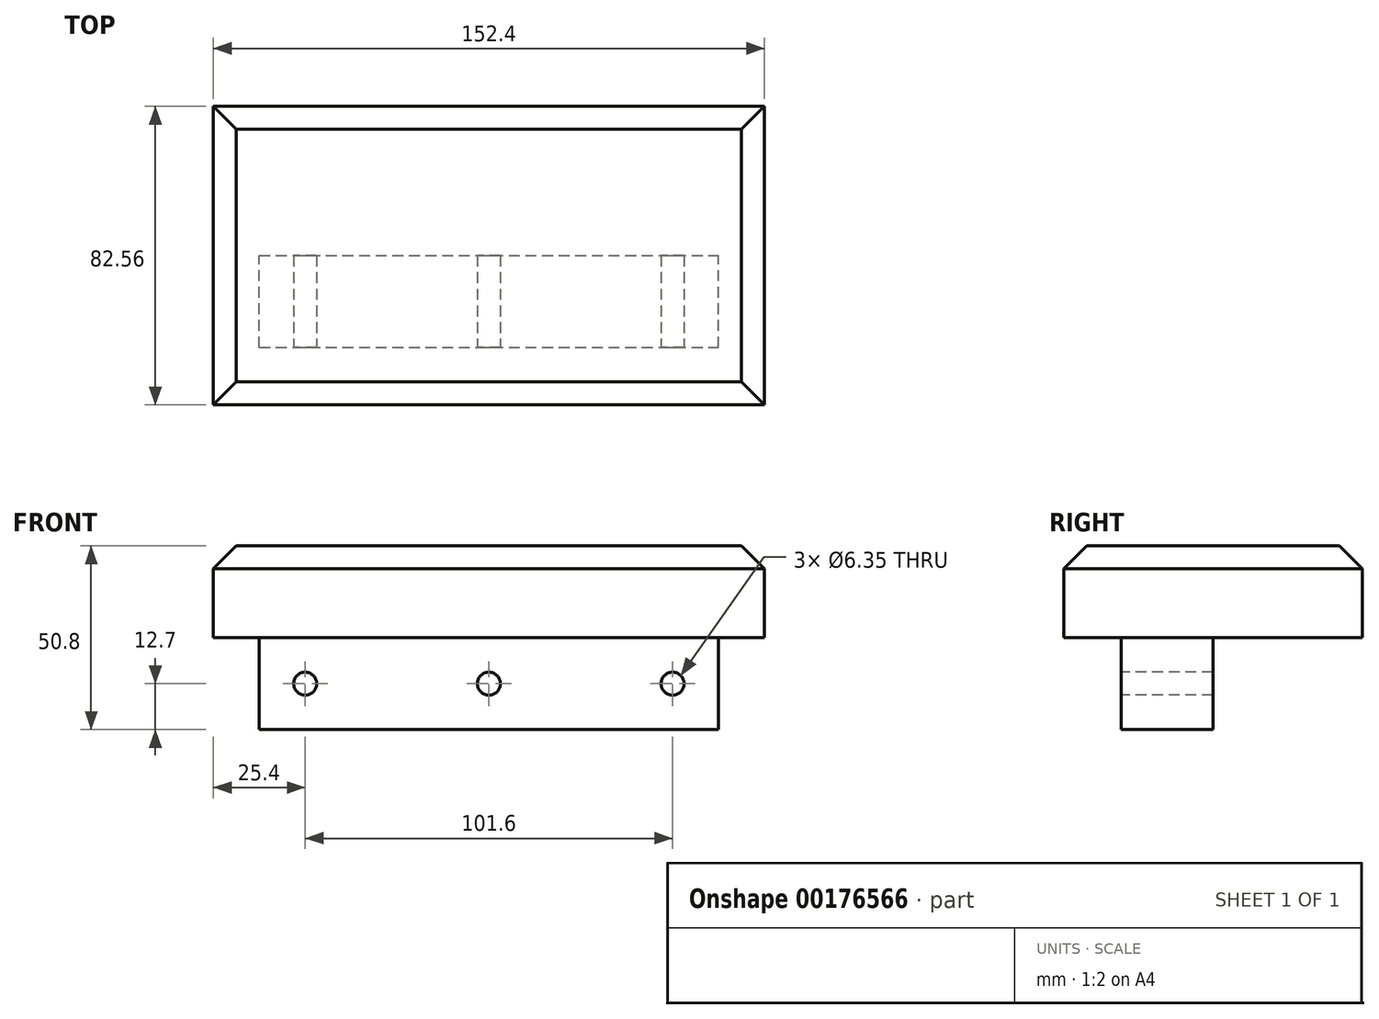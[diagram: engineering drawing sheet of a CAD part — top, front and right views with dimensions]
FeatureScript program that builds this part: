
annotation { "Feature Type Name" : "Feature", "Feature Type Description" : "" }
export const myFeature = defineFeature(function(context is Context, id is Id, definition is map)
    precondition{}
    {
        {
            var Q0;
            Q0=qCreatedBy(makeId("Top.planeOp"),FACE);
            var sketch = newSketch(context, id + "F0", { "sketchPlane" : qUnion([Q0])});
            skLineSegment(sketch, "E0.bottom", {"start": v(-76.2, 41.27) * mm, "end": v(76.2, 41.27) * mm});
            skLineSegment(sketch, "E0.top", {"start": v(-76.2, -41.27) * mm, "end": v(76.2, -41.27) * mm});
            skLineSegment(sketch, "E0.left", {"start": v(-76.2, 41.27) * mm, "end": v(-76.2, -41.27) * mm});
            skLineSegment(sketch, "E0.right", {"start": v(76.2, 41.27) * mm, "end": v(76.2, -41.27) * mm});
            skPoint(sketch, "E0.middle", {"position": v(0, 0) * mm});
            skSolve(sketch);
        }
        {
            var Q0;
            Q0 = qSketchRegion(id + "F0", true);
            extrude(context, id + "F1", {"entities" : qUnion([Q0]), "depth" : 25.4 * mm});
        }
        {
            var Q0;
            Q0=qCreatedBy(makeId("Front.planeOp"),FACE);
            var sketch = newSketch(context, id + "F2", { "sketchPlane" : qUnion([Q0])});
            skLineSegment(sketch, "E1", {"start": v(0, 0) * mm, "end": v(-63.5, 0) * mm});
            skLineSegment(sketch, "E2", {"start": v(0, 0) * mm, "end": v(63.5, 0) * mm});
            skLineSegment(sketch, "E3", {"start": v(-63.5, 0) * mm, "end": v(-63.5, -25.4) * mm});
            skLineSegment(sketch, "E4", {"start": v(63.5, 0) * mm, "end": v(63.5, -25.4) * mm});
            skLineSegment(sketch, "E5", {"start": v(-63.5, -25.4) * mm, "end": v(63.5, -25.4) * mm});
            skSolve(sketch);
        }
        {
            var Q0;
            Q0 = qSketchRegion(id + "F2", true);
            extrude(context, id + "F3", {"entities" : qUnion([Q0]), "operationType" : NewBodyOperationType.ADD, "depth" : 25.4 * mm});
        }
        {
            var Q0;
            Q0=makeQuery(id+"F3.opExtrude","CAP_FACE",FACE,{"disambiguationData":[OSD([sQuery(id+"F2.wireOp",EDGE,"E1"),sQuery(id+"F2.wireOp",EDGE,"E2"),sQuery(id+"F2.wireOp",EDGE,"E3"),sQuery(id+"F2.wireOp",EDGE,"E4"),sQuery(id+"F2.wireOp",EDGE,"E5")])],"isStart":false});
            var sketch = newSketch(context, id + "F4", { "sketchPlane" : qUnion([Q0])});
            skLineSegment(sketch, "E6", {"start": v(0, -12.7) * mm, "end": v(-50.8, -12.7) * mm});
            skPoint(sketch, "E6.startSnap0", {"position": v(-63.5, -12.7) * mm});
            skPoint(sketch, "E6.endSnap0", {"position": v(-63.5, -12.7) * mm});
            skCircle(sketch, "E7", {"center": v(-50.8, -12.7) * mm, "radius": 3.18 * mm});
            skCircle(sketch, "E8", {"center": v(0, -12.7) * mm, "radius": 3.18 * mm});
            skLineSegment(sketch, "E9", {"start": v(0, -12.7) * mm, "end": v(50.8, -12.7) * mm});
            skCircle(sketch, "E10", {"center": v(50.8, -12.7) * mm, "radius": 3.18 * mm});
            skSolve(sketch);
        }
        {
            var Q0;
            Q0 = qSketchRegion(id + "F4", true);
            extrude(context, id + "F5", {"entities" : qUnion([Q0]), "operationType" : NewBodyOperationType.REMOVE, "oppositeDirection" : true, "depth" : 25.4 * mm});
        }
        {
            var Q0;
            Q0=makeQuery(id+"F1.opExtrude","CAP_FACE",FACE,{"disambiguationData":[OSD([sQuery(id+"F0.wireOp",EDGE,"E0.bottom"),sQuery(id+"F0.wireOp",EDGE,"E0.top"),sQuery(id+"F0.wireOp",EDGE,"E0.left"),sQuery(id+"F0.wireOp",EDGE,"E0.right")])],"isStart":false});
            chamfer(context, id + "F6", {"entities" : qUnion([Q0]), "width" : 6.35 * mm, "tangentPropagation" : true});
        }
    });
